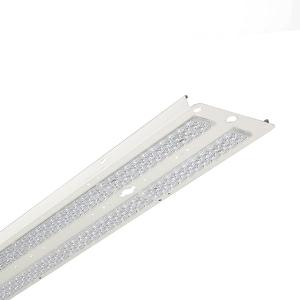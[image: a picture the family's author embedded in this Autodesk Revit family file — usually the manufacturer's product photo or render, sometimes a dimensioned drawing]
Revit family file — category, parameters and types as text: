
# Revit family: 3f_filippi_-_kit_led_retrofit_con_schermo_in_policarbonato_3f_filippi_-_a5215_-_kit_led_i3f_75_a3f_90_-__169ace065a06f042
name_source: partatom
category: Lighting Fixtures
units: mm (PartAtom-declared; Revit-internal decimal feet)

## family parameters
Cut with Voids When Loaded = No
Host = Face
Light Source = No
Part Type = Normal
Room Calculation Point = No
Round Connector Dimension = Use Diameter
Shared = No

## types (1)
- 3F Filippi - Kit LED Retrofit con schermo in policarbonato (1 x LED, 11519 lm, 74 W, 4000 K)
    Apparent Load = 74 VA
    Approval mark = ENEC
    CIE Flux Codes = 59 89 98 98 100
    Color Rendering = 80
    Color Temperature = 4000 K
    Control Gear = Electronic ballast
    Default Elevation = 1800 mm
    Description = Led retrofit kit suitable for Fluorescent Beta 2x i3F 76 and A3F 91 luminaires.

ILLUMINOTECHNICAL
Luminous efficiency 100% (DLOR 98%, ULOR 2%).
Initial luminous flux of the luminaire 11519 lm.
Wide symmetric distribution.
Installation Interdistance Transv.D = 1.40 x hu - Long.D = 1.45 x hu.
Tabular UGR (CIE 117 - 4H-8H; S=0.25H; 70/50/20): RUG 19.7 - 20.5.
Beam angle: 97° - 102°.
Luminous efficacy 156 lm/W.
Lifetime (L93/B10): 30000 h. (tq+25°C)
Lifetime (L90/B10): 50000 h. (tq+25°C)
Lifetime (L85/B10): 80000 h. (tq+25°C)
Lifetime (L80/B10): 100000 h. (tq+25°C)
Lifetime (L85/B10): 50000 h. (tq+40°C)
Sudden decreased luminous flux after 50000 hours: 0% (C0).
Photobiological safety in compliance with IEC/TR 62778: RG0 risk exempt, (IEC 62471).
In compliance with IEC/EN 62722-2-1 - IEC/EN 62717 standards.

SOURCE
2 linear LED modules 40W/840.
Energy efficiency class (UE 2019/2020 - UE 2019/2015): C.
CIE 13.3 Colour rendering index: CRI >80 (R9 <50%).
IES TM-30 Fidelity Index: Rf = 84 Rg = 95.
CCT nominal colour temperature 4000 K.
Colour initial tolerance (MacAdam): SDCM 3.

MECHANICAL
Diffuser in self-extinguishing V2 polycarbonate, photo-engraved interior, UV stabilised, injection moulded, with smooth outer surface, sealing gasket.
Gear-tray unit in hot-galvanised steel, painted in white polyester, fixed to the housing by means of "Ribloc" rapid devices in galvanised steel, hinged opening.
Lenses for wide distribution, in transparent methacrylate (PMMA) with external flat surface.
Luminaire with limited surface temperature. - D - (EN 60598-2-24)
Dimensions: 1565x235 mm, height 135 mm. Weight 4.635 kg.
Glow-wire test resistance 850°C.

ELECTRICAL
Halogen Free electronic wiring 230V-50/60Hz, power factor 0.95, THD <25%, constant output current, class I, 1 driver.
Power of the luminaire 74 W.
CE - IEC 60598-1 - EN 60598-1.
SAFE FLICKER: PstLM=<1 and SVM=<0.4 (IEC TR 61547-1 and IEC TR 63158), to ensure a more comfortable and safe light.
Luminaire compliant with EN 60598-2-22 for power supply from a centralised emergency system CPSS (Central Power Supply System), not incorporated in the luminaire - high risk areas excluded. The default power and flux are 100% in AC and 100% in DC.
Ambient temperature from -20°C to +40°C.
Temperature class T6 max 85°C.
Relative humidity UR: <85%.

INSTALLATION
Retrofit.
Correct installation of the retrofit LED kit, compliant with EN 60598-1 and CE marked, inside the 3F Filippi - Beta 2x i3F 75 and A3F 90 Fluorescent luminaires must be only carried out by qualified personnel to ensure compliance with the national installation standards.
Attention: to maintain the degree of protection of the device and for the purposes of validity of the guarantee of the new retrofit kits, it is imperative to replace the old cable guides (on the body of the device) with the new ones supplied.
All accessories dedicated to this product are available on the Catalog and on our website www.3F-Filippi.com.

WARNING
Fixture not suitable for cold stores with an ambient temperature <0°C and/or relative humidity >85%.
Luminaire designed for disposal/recycling at end-of-life.
Replaceable (LED only) light source by a professional. Replaceable control gear by a professional.
    Height = 135 mm
    Lamp = 1 x LED
    Lamp Light Flux = 11519 lm
    Lamp Power = 74 W
    Lamp count = 1
    Length = 1565 mm
    Lifetime = 50000 h
    Luminous efficacy = 156 lm/W
    Manufacturer = 3F Filippi
    ModVariant = No
    Model = 3F Filippi - A5215 - Kit LED i3F 75,A3F 90 - L1565 - L 2x40W AMPIO + PC
    Mounting Place = Ceiling
    Mounting Type = Surface mounted
    Number of Poles = 1
    OnlyDefault = Yes
    Power Factor = 1
    Product Name = 3F Filippi - Kit LED Retrofit con schermo in policarbonato
    Product group = ceiling mounted luminaire
    ProductGroupID = 3
    Protection Class = Protection class I
    Protection Degree = Degree of protection
    RLX_Detail_Level = 1
    RLX_Emergency_Light_Flux = 0 lm
    RLX_Emergency_Type = 0
    RLX_Emergency_Type_DB = No
    RlxData = <blob elided: 65305 chars, md5=e25c3c7d>
    Socket = socket
    Standby Power = 0 W
    System Light Flux = 11519 lm
    System Power = 74 W
    Type Comments = Product without accessories
    Type Image = 3ffilippi_a5215.jpg
    URL = http://relux.com
    VarID = ---
    Voltage = 0 V
    Weight = 0.00 kg
    Width = 235 mm

## geometry (parser evidence)
native form markers: Blend x4, Sweep x12
no freeform markers — native parametric forms only
